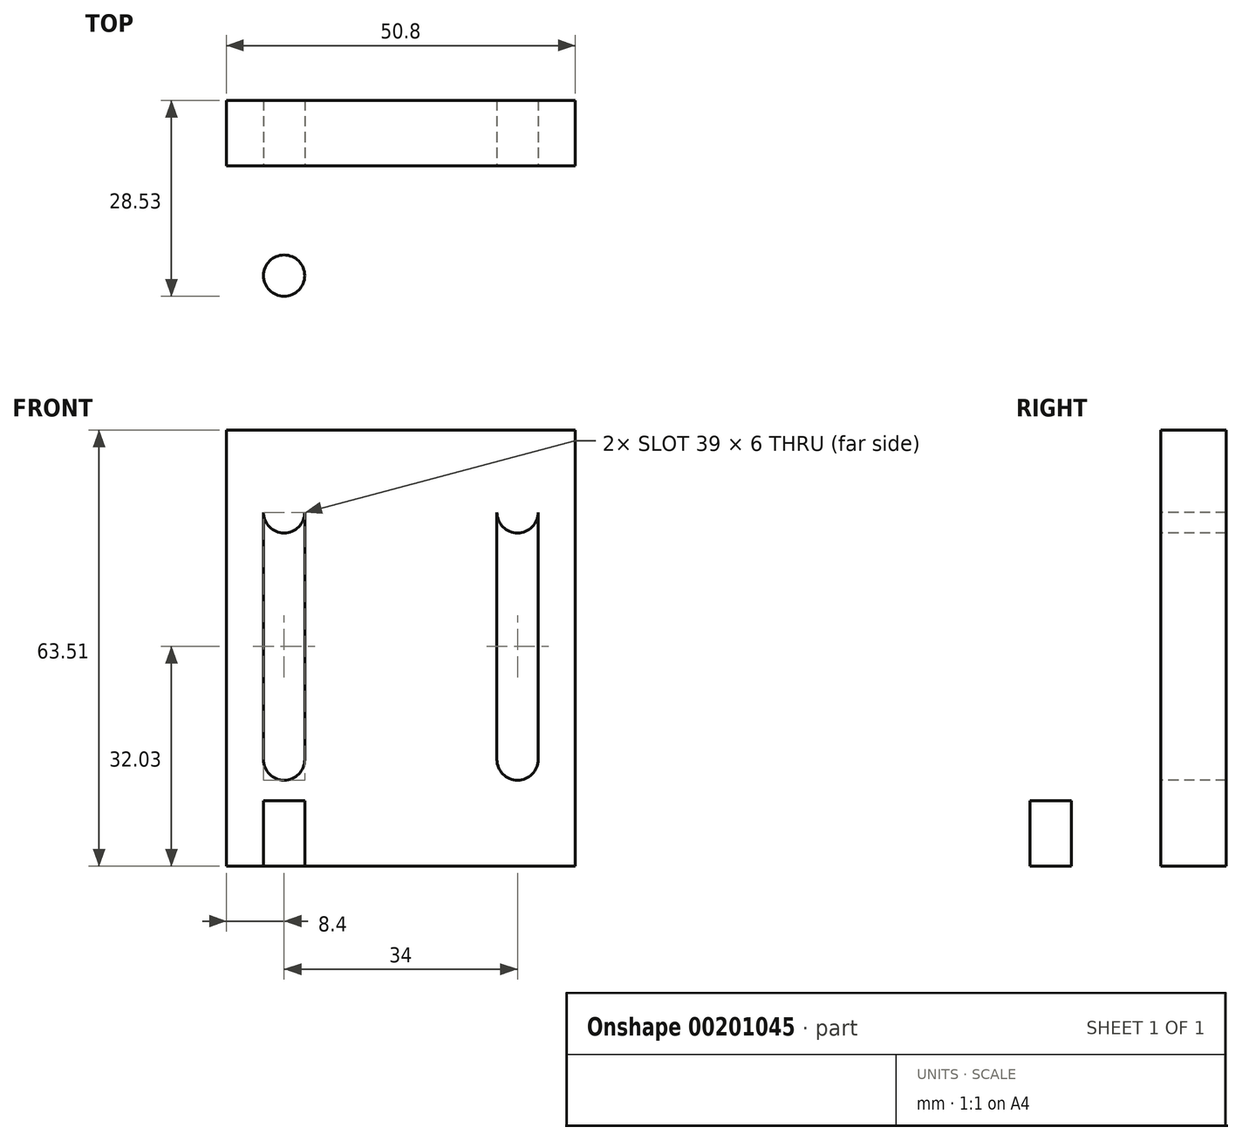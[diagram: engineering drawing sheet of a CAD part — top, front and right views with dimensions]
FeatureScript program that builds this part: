
annotation { "Feature Type Name" : "Feature", "Feature Type Description" : "" }
export const myFeature = defineFeature(function(context is Context, id is Id, definition is map)
    precondition{}
    {
        {
            var Q0;
            Q0=qCreatedBy(makeId("Right.planeOp"),FACE);
            var sketch = newSketch(context, id + "F0", { "sketchPlane" : qUnion([Q0])});
            skLineSegment(sketch, "E0.bottom", {"start": v(0, 0) * mm, "end": v(9.53, 0) * mm});
            skLineSegment(sketch, "E0.top", {"start": v(0, 53.98) * mm, "end": v(9.52, 53.98) * mm});
            skLineSegment(sketch, "E0.left", {"start": v(0, 0) * mm, "end": v(0, 53.98) * mm});
            skLineSegment(sketch, "E0.right", {"start": v(9.53, 0) * mm, "end": v(9.52, 53.98) * mm});
            skLineSegment(sketch, "E1.bottom", {"start": v(9.53, 0) * mm, "end": v(-53.97, 0) * mm});
            skLineSegment(sketch, "E1.top", {"start": v(9.53, -9.52) * mm, "end": v(-53.97, -9.52) * mm});
            skLineSegment(sketch, "E1.left", {"start": v(9.53, 0) * mm, "end": v(9.53, -9.52) * mm});
            skLineSegment(sketch, "E1.right", {"start": v(-53.97, 0) * mm, "end": v(-53.97, -9.52) * mm});
            skSolve(sketch);
        }
        {
            var Q0;
            Q0=qCreatedBy(makeId("Front.planeOp"),FACE);
            var sketch = newSketch(context, id + "F1", { "sketchPlane" : qUnion([Q0])});
            skLineSegment(sketch, "E2.bottom", {"start": v(-25.4, -9.52) * mm, "end": v(25.4, -9.53) * mm});
            skLineSegment(sketch, "E2.top", {"start": v(-25.4, 53.97) * mm, "end": v(25.4, 53.97) * mm});
            skLineSegment(sketch, "E2.left", {"start": v(-25.4, -9.53) * mm, "end": v(-25.4, 53.97) * mm});
            skLineSegment(sketch, "E2.right", {"start": v(25.4, -9.53) * mm, "end": v(25.4, 53.97) * mm});
            skLineSegment(sketch, "E3", {"start": v(-25.4, 0) * mm, "end": v(25.4, 0) * mm});
            skLineSegment(sketch, "E4", {"start": v(17, 45) * mm, "end": v(17, 3) * mm});
            skLineSegment(sketch, "E5.MirrorCS", {"start": v(-17, 45) * mm, "end": v(-17, 3) * mm});
            skCircle(sketch, "E6", {"center": v(-17, 42) * mm, "radius": 3 * mm});
            skCircle(sketch, "E7", {"center": v(-17, 6) * mm, "radius": 3 * mm});
            skLineSegment(sketch, "E8", {"start": v(-20, 6) * mm, "end": v(-20, 42) * mm});
            skLineSegment(sketch, "E9", {"start": v(-14, 6) * mm, "end": v(-14, 42) * mm});
            skCircle(sketch, "E10.MirrorC", {"center": v(17, 42) * mm, "radius": 3 * mm});
            skLineSegment(sketch, "E11.MirrorCS", {"start": v(14, 6) * mm, "end": v(14, 42) * mm});
            skLineSegment(sketch, "E12.MirrorCS", {"start": v(20, 6) * mm, "end": v(20, 42) * mm});
            skCircle(sketch, "E13.MirrorC", {"center": v(17, 6) * mm, "radius": 3 * mm});
            skSolve(sketch);
        }
        {
            var Q0;
            Q0=qCreatedBy(makeId("Top.planeOp"),FACE);
            var sketch = newSketch(context, id + "F2", { "sketchPlane" : qUnion([Q0])});
            skLineSegment(sketch, "E14.bottom", {"start": v(-25.4, -53.97) * mm, "end": v(25.4, -53.97) * mm});
            skLineSegment(sketch, "E14.top", {"start": v(-25.4, 9.52) * mm, "end": v(25.4, 9.53) * mm});
            skLineSegment(sketch, "E14.left", {"start": v(-25.4, -53.97) * mm, "end": v(-25.4, 9.53) * mm});
            skLineSegment(sketch, "E14.right", {"start": v(25.4, -53.97) * mm, "end": v(25.4, 9.53) * mm});
            skLineSegment(sketch, "E15", {"start": v(-25.4, 0) * mm, "end": v(25.4, 0) * mm});
            skCircle(sketch, "E16", {"center": v(17, -16) * mm, "radius": 3 * mm});
            skCircle(sketch, "E17.MirrorC", {"center": v(-17, -16) * mm, "radius": 3 * mm});
            skSolve(sketch);
        }
        {
            var Q0;
            Q0=makeQuery(id+"F0.imprint","IMPRINT",FACE,{"disambiguationData":[TD([[makeQuery(id+"F0.imprint","IMPRINT",EDGE,{"derivedFrom":sQuery(id+"F0.wireOp",EDGE,"E1.top")}),-1.0]])]});
            var Q1;
            Q1=makeQuery(id+"F0.imprint","IMPRINT",FACE,{"disambiguationData":[TD([[makeQuery(id+"F0.imprint","IMPRINT",EDGE,{"derivedFrom":sQuery(id+"F0.wireOp",EDGE,"E0.top")}),-1.0]])]});
            extrude(context, id + "F3", {"entities" : qUnion([Q0, Q1]), "endBound" : BoundingType.SYMMETRIC, "depth" : 50.8 * mm});
        }
        {
            var Q0;
            {var subQ0=sQuery(id+"F1.wireOp",EDGE,"E7");var subQ1=sQuery(id+"F1.wireOp",EDGE,"E5.MirrorCS");var subQ2=makeQuery(id+"F1.imprint","INTERSECT",VERTEX,{"disambiguationData":[OD(0.0)],"derivedFrom":[subQ1,subQ0]});Q0=makeQuery(id+"F1.imprint","IMPRINT",FACE,{"disambiguationData":[TD([[makeQuery(id+"F1.imprint","IMPRINT",EDGE,{"disambiguationData":[TD([[subQ2,1.0]])],"derivedFrom":subQ1}),1.0]])]});}
            var Q1;
            {var subQ0=sQuery(id+"F1.wireOp",EDGE,"E7");var subQ1=sQuery(id+"F1.wireOp",EDGE,"E5.MirrorCS");var subQ2=makeQuery(id+"F1.imprint","INTERSECT",VERTEX,{"disambiguationData":[OD(0.0)],"derivedFrom":[subQ1,subQ0]});Q1=makeQuery(id+"F1.imprint","IMPRINT",FACE,{"disambiguationData":[TD([[makeQuery(id+"F1.imprint","IMPRINT",EDGE,{"disambiguationData":[TD([[subQ2,1.0]])],"derivedFrom":subQ1}),-1.0]])]});}
            var Q2;
            {var subQ5=sQuery(id+"F1.wireOp",EDGE,"E8");Q2=makeQuery(id+"F1.imprint","IMPRINT",FACE,{"disambiguationData":[TD([[makeQuery(id+"F1.imprint","IMPRINT",EDGE,{"derivedFrom":subQ5}),-1.0]])]});}
            var Q3;
            {var subQ5=sQuery(id+"F1.wireOp",EDGE,"E9");Q3=makeQuery(id+"F1.imprint","IMPRINT",FACE,{"disambiguationData":[TD([[makeQuery(id+"F1.imprint","IMPRINT",EDGE,{"derivedFrom":subQ5}),1.0]])]});}
            var Q4;
            {var subQ0=sQuery(id+"F1.wireOp",EDGE,"E6");var subQ1=sQuery(id+"F1.wireOp",EDGE,"E5.MirrorCS");var subQ2=makeQuery(id+"F1.imprint","INTERSECT",VERTEX,{"disambiguationData":[OD(0.0)],"derivedFrom":[subQ1,subQ0]});Q4=makeQuery(id+"F1.imprint","IMPRINT",FACE,{"disambiguationData":[TD([[makeQuery(id+"F1.imprint","IMPRINT",EDGE,{"disambiguationData":[TD([[subQ2,-1.0]])],"derivedFrom":subQ1}),1.0]])]});}
            var Q5;
            {var subQ0=sQuery(id+"F1.wireOp",EDGE,"E6");var subQ1=sQuery(id+"F1.wireOp",EDGE,"E5.MirrorCS");var subQ2=makeQuery(id+"F1.imprint","INTERSECT",VERTEX,{"disambiguationData":[OD(0.0)],"derivedFrom":[subQ1,subQ0]});Q5=makeQuery(id+"F1.imprint","IMPRINT",FACE,{"disambiguationData":[TD([[makeQuery(id+"F1.imprint","IMPRINT",EDGE,{"disambiguationData":[TD([[subQ2,-1.0]])],"derivedFrom":subQ1}),-1.0]])]});}
            var Q6;
            {var subQ0=sQuery(id+"F1.wireOp",EDGE,"E10.MirrorC");var subQ1=sQuery(id+"F1.wireOp",EDGE,"E4");var subQ2=makeQuery(id+"F1.imprint","INTERSECT",VERTEX,{"disambiguationData":[OD(0.0)],"derivedFrom":[subQ1,subQ0]});Q6=makeQuery(id+"F1.imprint","IMPRINT",FACE,{"disambiguationData":[TD([[makeQuery(id+"F1.imprint","IMPRINT",EDGE,{"disambiguationData":[TD([[subQ2,-1.0]])],"derivedFrom":subQ1}),1.0]])]});}
            var Q7;
            {var subQ0=sQuery(id+"F1.wireOp",EDGE,"E10.MirrorC");var subQ1=sQuery(id+"F1.wireOp",EDGE,"E4");var subQ2=makeQuery(id+"F1.imprint","INTERSECT",VERTEX,{"disambiguationData":[OD(0.0)],"derivedFrom":[subQ1,subQ0]});Q7=makeQuery(id+"F1.imprint","IMPRINT",FACE,{"disambiguationData":[TD([[makeQuery(id+"F1.imprint","IMPRINT",EDGE,{"disambiguationData":[TD([[subQ2,-1.0]])],"derivedFrom":subQ1}),-1.0]])]});}
            var Q8;
            {var subQ5=sQuery(id+"F1.wireOp",EDGE,"E11.MirrorCS");Q8=makeQuery(id+"F1.imprint","IMPRINT",FACE,{"disambiguationData":[TD([[makeQuery(id+"F1.imprint","IMPRINT",EDGE,{"derivedFrom":subQ5}),-1.0]])]});}
            var Q9;
            {var subQ5=sQuery(id+"F1.wireOp",EDGE,"E12.MirrorCS");Q9=makeQuery(id+"F1.imprint","IMPRINT",FACE,{"disambiguationData":[TD([[makeQuery(id+"F1.imprint","IMPRINT",EDGE,{"derivedFrom":subQ5}),1.0]])]});}
            var Q10;
            {var subQ0=sQuery(id+"F1.wireOp",EDGE,"E13.MirrorC");var subQ1=sQuery(id+"F1.wireOp",EDGE,"E4");var subQ2=makeQuery(id+"F1.imprint","INTERSECT",VERTEX,{"disambiguationData":[OD(0.0)],"derivedFrom":[subQ1,subQ0]});Q10=makeQuery(id+"F1.imprint","IMPRINT",FACE,{"disambiguationData":[TD([[makeQuery(id+"F1.imprint","IMPRINT",EDGE,{"disambiguationData":[TD([[subQ2,1.0]])],"derivedFrom":subQ1}),1.0]])]});}
            var Q11;
            {var subQ0=sQuery(id+"F1.wireOp",EDGE,"E13.MirrorC");var subQ1=sQuery(id+"F1.wireOp",EDGE,"E4");var subQ2=makeQuery(id+"F1.imprint","INTERSECT",VERTEX,{"disambiguationData":[OD(0.0)],"derivedFrom":[subQ1,subQ0]});Q11=makeQuery(id+"F1.imprint","IMPRINT",FACE,{"disambiguationData":[TD([[makeQuery(id+"F1.imprint","IMPRINT",EDGE,{"disambiguationData":[TD([[subQ2,1.0]])],"derivedFrom":subQ1}),-1.0]])]});}
            extrude(context, id + "F4", {"entities" : qUnion([Q0, Q1, Q2, Q3, Q4, Q5, Q6, Q7, Q8, Q9, Q10, Q11]), "operationType" : NewBodyOperationType.REMOVE, "endBound" : BoundingType.THROUGH_ALL, "oppositeDirection" : true, "depth" : 25.4 * mm});
        }
        {
            var Q0;
            Q0=makeQuery(id+"F2.imprint","IMPRINT",FACE,{"disambiguationData":[TD([[makeQuery(id+"F2.imprint","IMPRINT",EDGE,{"derivedFrom":sQuery(id+"F2.wireOp",EDGE,"E17.MirrorC")}),-1.0]])]});
            var Q1;
            Q1=makeQuery(id+"F2.imprint","IMPRINT",FACE,{"disambiguationData":[TD([[makeQuery(id+"F2.imprint","IMPRINT",EDGE,{"derivedFrom":sQuery(id+"F2.wireOp",EDGE,"E16")}),1.0]])]});
            extrude(context, id + "F5", {"entities" : qUnion([Q0, Q1]), "operationType" : NewBodyOperationType.REMOVE, "endBound" : BoundingType.THROUGH_ALL, "oppositeDirection" : true, "depth" : 25.4 * mm});
        }
    });
